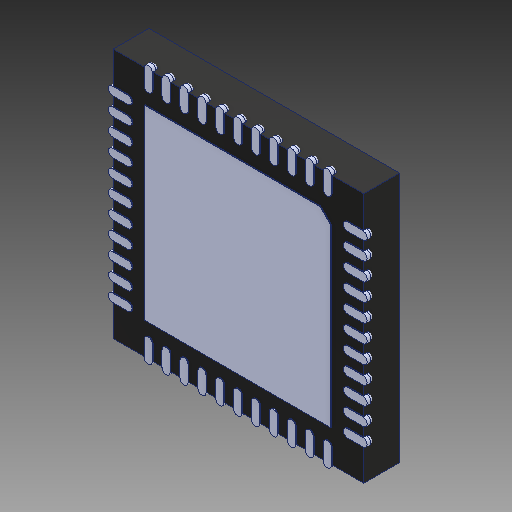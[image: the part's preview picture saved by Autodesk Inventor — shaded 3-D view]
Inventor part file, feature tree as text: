
AUTODESK INVENTOR PART (.ipt)
format: ipt  version: 2018 (Build 220112000, 112)  size: 1,385,984 bytes
history: native  units: mm
features: chamfer x1
ambient origin geometry x8: Origin, YZ Plane, XZ Plane, XY Plane, X Axis, Y Axis, Z Axis, Center Point
bodies: Volumenkörper1 (feature_tree)
feature tree (1):
  chamfer  "Chamfer1"  [1 undecoded]
note: 1 required parameter value undecoded (feature->parameter linkage not recoverable at this tier; creation-order binding heuristic only, values carry confidence <= 0.55)
